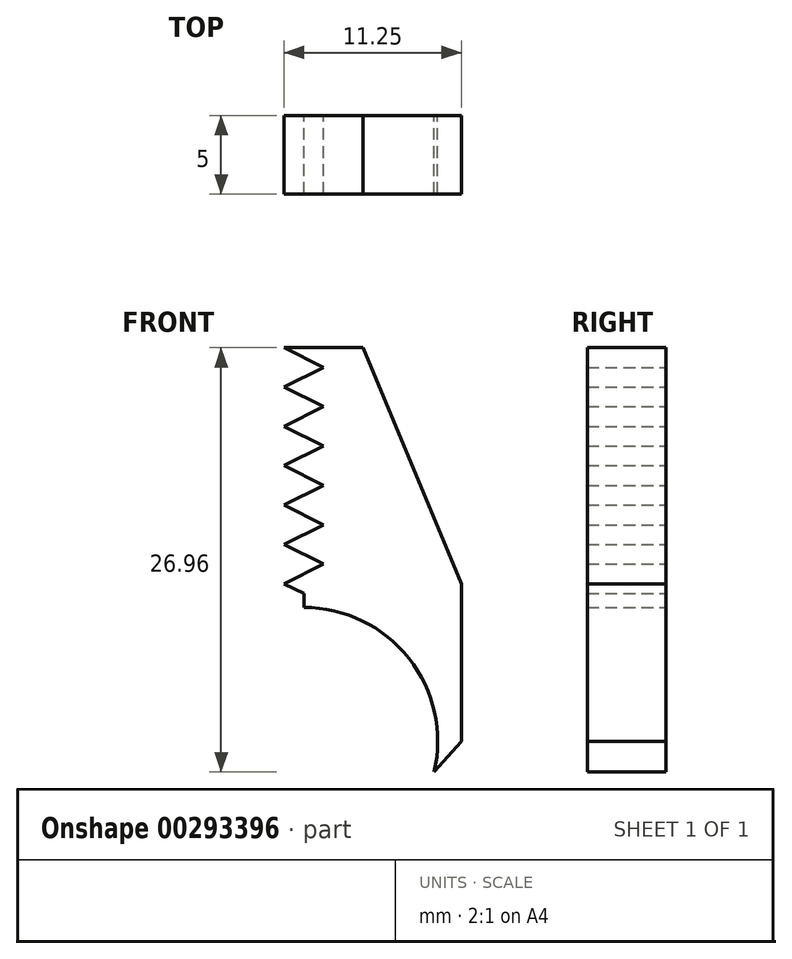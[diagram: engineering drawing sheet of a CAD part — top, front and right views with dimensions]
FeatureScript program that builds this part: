
annotation { "Feature Type Name" : "Feature", "Feature Type Description" : "" }
export const myFeature = defineFeature(function(context is Context, id is Id, definition is map)
    precondition{}
    {
        {
            var Q0;
            Q0=qCreatedBy(makeId("Front.planeOp"),FACE);
            var sketch = newSketch(context, id + "F0", { "sketchPlane" : qUnion([Q0])});
            skArc(sketch, "E0", {"start": v(0, 7.5) * mm, "mid": v(-6.84, -3.09) * mm, "end": v(5.63, -4.96) * mm});
            skLineSegment(sketch, "E1", {"start": v(0, 7.5) * mm, "end": v(0, 9.13) * mm});
            skLineSegment(sketch, "E2", {"start": v(0, 9.13) * mm, "end": v(1.25, 10) * mm});
            skLineSegment(sketch, "E3", {"start": v(1.25, 10) * mm, "end": v(1.25, 25) * mm});
            skLineSegment(sketch, "E4", {"start": v(1.25, 25) * mm, "end": v(3.75, 25) * mm});
            skLineSegment(sketch, "E5", {"start": v(3.75, 25) * mm, "end": v(10, 10) * mm});
            skLineSegment(sketch, "E6", {"start": v(10, 10) * mm, "end": v(10, 0) * mm});
            skLineSegment(sketch, "E7", {"start": v(10, 0) * mm, "end": v(5.62, -4.96) * mm});
            skLineSegment(sketch, "E8", {"start": v(1.25, 25) * mm, "end": v(1.25, 10) * mm});
            skLineSegment(sketch, "E9", {"start": v(1.25, 10) * mm, "end": v(10, 10) * mm, "construction": true});
            skLineSegment(sketch, "E10", {"start": v(0, 0) * mm, "end": v(10, 0) * mm, "construction": true});
            skLineSegment(sketch, "E11", {"start": v(0, 9.13) * mm, "end": v(0, 25) * mm, "construction": true});
            skSolve(sketch);
        }
        {
            var Q0;
            Q0=makeQuery(id+"F0.imprint","IMPRINT",FACE,{"disambiguationData":[TD([[makeQuery(id+"F0.imprint","IMPRINT",EDGE,{"derivedFrom":sQuery(id+"F0.wireOp",EDGE,"E0")}),1.0]])]});
            extrude(context, id + "F1", {"entities" : qUnion([Q0]), "depth" : 5 * mm});
        }
        {
            var Q0;
            Q0=makeQuery(id+"F1.opExtrude","CAP_FACE",FACE,{"disambiguationData":[OSD([sQuery(id+"F0.wireOp",EDGE,"E0"),sQuery(id+"F0.wireOp",EDGE,"E1"),sQuery(id+"F0.wireOp",EDGE,"E2"),sQuery(id+"F0.wireOp",EDGE,"E4"),sQuery(id+"F0.wireOp",EDGE,"E5"),sQuery(id+"F0.wireOp",EDGE,"E6"),sQuery(id+"F0.wireOp",EDGE,"E7"),sQuery(id+"F0.wireOp",EDGE,"E8")])],"isStart":false});
            var sketch = newSketch(context, id + "F2", { "sketchPlane" : qUnion([Q0])});
            skLineSegment(sketch, "E12", {"start": v(1.25, 25) * mm, "end": v(1.25, 22.5) * mm});
            skLineSegment(sketch, "E13", {"start": v(1.25, 23.75) * mm, "end": v(-1.25, 25) * mm});
            skPoint(sketch, "E13.endSnap0", {"position": v(1.25, 23.75) * mm});
            skLineSegment(sketch, "E14", {"start": v(1.25, 9.13) * mm, "end": v(1.25, 24.37) * mm, "construction": true});
            skLineSegment(sketch, "E15.0.1.0", {"start": v(-1.25, 22.5) * mm, "end": v(1.25, 23.75) * mm});
            skLineSegment(sketch, "E15.0.1.1", {"start": v(1.25, 21.25) * mm, "end": v(-1.25, 22.5) * mm});
            skLineSegment(sketch, "E15.0.1.2", {"start": v(0, 6.63) * mm, "end": v(0, 7.5) * mm, "construction": true});
            skLineSegment(sketch, "E15.0.2.0", {"start": v(-1.25, 20) * mm, "end": v(1.25, 21.25) * mm});
            skLineSegment(sketch, "E15.0.2.1", {"start": v(1.25, 18.75) * mm, "end": v(-1.25, 20) * mm});
            skLineSegment(sketch, "E15.0.2.2", {"start": v(0, 4.13) * mm, "end": v(0, 8.5) * mm, "construction": true});
            skLineSegment(sketch, "E15.0.3.0", {"start": v(-1.25, 17.5) * mm, "end": v(1.25, 18.75) * mm});
            skLineSegment(sketch, "E15.0.3.1", {"start": v(1.25, 16.25) * mm, "end": v(-1.25, 17.5) * mm});
            skLineSegment(sketch, "E15.0.3.2", {"start": v(0, 1.63) * mm, "end": v(0, 8.5) * mm, "construction": true});
            skLineSegment(sketch, "E15.0.4.0", {"start": v(-1.25, 15) * mm, "end": v(1.25, 16.25) * mm});
            skLineSegment(sketch, "E15.0.4.1", {"start": v(1.25, 13.75) * mm, "end": v(-1.25, 15) * mm});
            skLineSegment(sketch, "E15.0.4.2", {"start": v(0, -0.87) * mm, "end": v(0, 7.5) * mm, "construction": true});
            skLineSegment(sketch, "E15.0.5.0", {"start": v(-1.25, 12.5) * mm, "end": v(1.25, 13.75) * mm});
            skLineSegment(sketch, "E15.0.5.1", {"start": v(1.25, 11.25) * mm, "end": v(-1.25, 12.5) * mm});
            skLineSegment(sketch, "E15.0.5.2", {"start": v(0, -3.37) * mm, "end": v(0, 9.13) * mm, "construction": true});
            skLineSegment(sketch, "E15.direction1", {"start": v(0, 9.13) * mm, "end": v(25, 9.13) * mm, "construction": true});
            skLineSegment(sketch, "E15.direction2", {"start": v(0, 8.5) * mm, "end": v(0, 6.63) * mm, "construction": true});
            skCircle(sketch, "E16", {"center": v(0, 0) * mm, "radius": 7.5 * mm, "construction": true});
            skArc(sketch, "E17.0", {"start": v(8.27, -1.96) * mm, "mid": v(6.67, 5.27) * mm, "end": v(0, 8.5) * mm});
            skLineSegment(sketch, "E18", {"start": v(10, 0) * mm, "end": v(5.63, -4.96) * mm});
            skLineSegment(sketch, "E19.trimOffspring", {"start": v(0, 11.05) * mm, "end": v(0, 24.37) * mm, "construction": true});
            skLineSegment(sketch, "E20.trimOffspring", {"start": v(0, 8.55) * mm, "end": v(0, 9.13) * mm, "construction": true});
            skLineSegment(sketch, "E21", {"start": v(0, 9.13) * mm, "end": v(0, 8.5) * mm});
            skLineSegment(sketch, "E22", {"start": v(10, 0) * mm, "end": v(10, 10) * mm});
            skLineSegment(sketch, "E23", {"start": v(10, 10) * mm, "end": v(3.75, 25) * mm});
            skLineSegment(sketch, "E24", {"start": v(3.75, 25) * mm, "end": v(1.25, 25) * mm});
            skLineSegment(sketch, "E25", {"start": v(1.25, 25) * mm, "end": v(-1.25, 25) * mm});
            skLineSegment(sketch, "E26", {"start": v(1.25, 11.25) * mm, "end": v(1.25, 9.13) * mm, "construction": true});
            skLineSegment(sketch, "E27", {"start": v(1.25, 9.13) * mm, "end": v(1.25, 11.25) * mm, "construction": true});
            skLineSegment(sketch, "E28.0.1.0", {"start": v(-1.25, 10) * mm, "end": v(1.25, 11.25) * mm});
            skLineSegment(sketch, "E28.0.1.1", {"start": v(0, 9.37) * mm, "end": v(-1.25, 10) * mm});
            skLineSegment(sketch, "E28.1.0.0", {"start": v(16.35, 12.5) * mm, "end": v(18.85, 13.75) * mm});
            skLineSegment(sketch, "E28.1.0.1", {"start": v(18.85, 11.25) * mm, "end": v(16.35, 12.5) * mm});
            skLineSegment(sketch, "E28.1.1.0", {"start": v(16.35, 10) * mm, "end": v(18.85, 11.25) * mm});
            skLineSegment(sketch, "E28.1.1.1", {"start": v(18.85, 8.75) * mm, "end": v(16.35, 10) * mm});
            skLineSegment(sketch, "E28.2.0.0", {"start": v(33.95, 12.5) * mm, "end": v(36.45, 13.75) * mm});
            skLineSegment(sketch, "E28.2.0.1", {"start": v(36.45, 11.25) * mm, "end": v(33.95, 12.5) * mm});
            skLineSegment(sketch, "E28.2.1.0", {"start": v(33.95, 10) * mm, "end": v(36.45, 11.25) * mm});
            skLineSegment(sketch, "E28.2.1.1", {"start": v(36.45, 8.75) * mm, "end": v(33.95, 10) * mm});
            skLineSegment(sketch, "E28.direction1", {"start": v(-1.25, 12.5) * mm, "end": v(16.35, 12.5) * mm, "construction": true});
            skLineSegment(sketch, "E28.direction2", {"start": v(-1.25, 12.5) * mm, "end": v(-1.25, 10) * mm, "construction": true});
            skPoint(sketch, "E29.orphan", {"position": v(1.25, 8.75) * mm});
            skLineSegment(sketch, "E30.trimOffspring", {"start": v(0, 9.37) * mm, "end": v(0, 16.87) * mm, "construction": true});
            skLineSegment(sketch, "E31.trimOffspring", {"start": v(0, 9.37) * mm, "end": v(0, 19.37) * mm, "construction": true});
            skLineSegment(sketch, "E32.trimOffspring", {"start": v(0, 9.37) * mm, "end": v(0, 11.87) * mm, "construction": true});
            skLineSegment(sketch, "E33.trimOffspring", {"start": v(0, 9.37) * mm, "end": v(0, 14.37) * mm, "construction": true});
            skLineSegment(sketch, "E34", {"start": v(0, 9.37) * mm, "end": v(0, 9.13) * mm});
            skSolve(sketch);
        }
        {
            var Q0;
            Q0=qSketchRegion(id+"F2",true);
            extrude(context, id + "F3", {"entities" : qUnion([Q0]), "operationType" : NewBodyOperationType.ADD, "depth" : 5 * mm, "hasSecondDirection" : true, "secondDirectionOppositeDirection" : true, "secondDirectionDepth" : 5 * mm});
        }
        {
            var Q0;
            Q0=makeQuery(id+"F1.opExtrude","CAP_FACE",FACE,{"disambiguationData":[OSD([sQuery(id+"F0.wireOp",EDGE,"E0"),sQuery(id+"F0.wireOp",EDGE,"E1"),sQuery(id+"F0.wireOp",EDGE,"E2"),sQuery(id+"F0.wireOp",EDGE,"E4"),sQuery(id+"F0.wireOp",EDGE,"E5"),sQuery(id+"F0.wireOp",EDGE,"E6"),sQuery(id+"F0.wireOp",EDGE,"E7"),sQuery(id+"F0.wireOp",EDGE,"E8")])],"isStart":false});
            var sketch = newSketch(context, id + "F4", { "sketchPlane" : qUnion([Q0])});
            skCircle(sketch, "E35", {"center": v(0, 0) * mm, "radius": 2.5 * mm});
            skSolve(sketch);
        }
        {
            var Q0;
            Q0=makeQuery(id+"F4.imprint","IMPRINT",FACE,{"disambiguationData":[TD([[makeQuery(id+"F4.imprint","IMPRINT",EDGE,{"derivedFrom":sQuery(id+"F4.wireOp",EDGE,"E35")}),1.0]])]});
            extrude(context, id + "F5", {"entities" : qUnion([Q0]), "operationType" : NewBodyOperationType.REMOVE, "endBound" : BoundingType.THROUGH_ALL, "oppositeDirection" : true, "depth" : 25 * mm});
        }
        {
            var Q0;
            Q0=makeQuery(id+"F1.opExtrude","SWEPT_BODY",BODY,{"disambiguationData":[OSD([sQuery(id+"F0.wireOp",EDGE,"E0"),sQuery(id+"F0.wireOp",EDGE,"E1"),sQuery(id+"F0.wireOp",EDGE,"E2"),sQuery(id+"F0.wireOp",EDGE,"E4"),sQuery(id+"F0.wireOp",EDGE,"E5"),sQuery(id+"F0.wireOp",EDGE,"E6"),sQuery(id+"F0.wireOp",EDGE,"E7"),sQuery(id+"F0.wireOp",EDGE,"E8")])]});
            transform(context, id + "F6", {"entities" : qUnion([Q0]), "transformType" : TransformType.TRANSLATION_3D, "dx" : 0 * mm, "dy" : 0 * mm, "dz" : 0 * mm, "makeCopy" : true});
        }
        {
            var Q0;
            Q0=makeQuery(id+"F6.opPattern","COPY",BODY,{"derivedFrom":makeQuery(id+"F1.opExtrude","SWEPT_BODY",BODY,{"disambiguationData":[OSD([sQuery(id+"F0.wireOp",EDGE,"E0"),sQuery(id+"F0.wireOp",EDGE,"E1"),sQuery(id+"F0.wireOp",EDGE,"E2"),sQuery(id+"F0.wireOp",EDGE,"E4"),sQuery(id+"F0.wireOp",EDGE,"E5"),sQuery(id+"F0.wireOp",EDGE,"E6"),sQuery(id+"F0.wireOp",EDGE,"E7"),sQuery(id+"F0.wireOp",EDGE,"E8")])]}),"instanceName":"1"});
            deleteBodies(context, id + "F7", {"entities" : qUnion([Q0])});
        }
        {
            var Q0;
            Q0=makeQuery(id+"F1.opExtrude","SWEPT_BODY",BODY,{"disambiguationData":[OSD([sQuery(id+"F0.wireOp",EDGE,"E0"),sQuery(id+"F0.wireOp",EDGE,"E1"),sQuery(id+"F0.wireOp",EDGE,"E2"),sQuery(id+"F0.wireOp",EDGE,"E4"),sQuery(id+"F0.wireOp",EDGE,"E5"),sQuery(id+"F0.wireOp",EDGE,"E6"),sQuery(id+"F0.wireOp",EDGE,"E7"),sQuery(id+"F0.wireOp",EDGE,"E8")])]});
            transform(context, id + "F8", {"entities" : qUnion([Q0]), "transformType" : TransformType.TRANSLATION_3D, "dx" : 20 * mm, "dy" : 0 * mm, "dz" : 0 * mm, "makeCopy" : true});
        }
        {
            var Q0;
            Q0=makeQuery(id+"F8.opPattern","COPY",BODY,{"derivedFrom":makeQuery(id+"F1.opExtrude","SWEPT_BODY",BODY,{"disambiguationData":[OSD([sQuery(id+"F0.wireOp",EDGE,"E0"),sQuery(id+"F0.wireOp",EDGE,"E1"),sQuery(id+"F0.wireOp",EDGE,"E2"),sQuery(id+"F0.wireOp",EDGE,"E4"),sQuery(id+"F0.wireOp",EDGE,"E5"),sQuery(id+"F0.wireOp",EDGE,"E6"),sQuery(id+"F0.wireOp",EDGE,"E7"),sQuery(id+"F0.wireOp",EDGE,"E8")])]}),"instanceName":"1"});
            deleteBodies(context, id + "F9", {"entities" : qUnion([Q0])});
        }
        {
            var Q0;
            Q0=makeQuery(id+"F1.opExtrude","SWEPT_BODY",BODY,{"disambiguationData":[OSD([sQuery(id+"F0.wireOp",EDGE,"E0"),sQuery(id+"F0.wireOp",EDGE,"E1"),sQuery(id+"F0.wireOp",EDGE,"E2"),sQuery(id+"F0.wireOp",EDGE,"E4"),sQuery(id+"F0.wireOp",EDGE,"E5"),sQuery(id+"F0.wireOp",EDGE,"E6"),sQuery(id+"F0.wireOp",EDGE,"E7"),sQuery(id+"F0.wireOp",EDGE,"E8")])]});
            transform(context, id + "F10", {"entities" : qUnion([Q0]), "transformType" : TransformType.TRANSLATION_3D, "dx" : 0 * mm, "dy" : 0 * mm, "dz" : 0 * mm, "makeCopy" : true});
        }
        {
            var Q0;
            Q0=makeQuery(id+"F10.opPattern","COPY",BODY,{"derivedFrom":makeQuery(id+"F1.opExtrude","SWEPT_BODY",BODY,{"disambiguationData":[OSD([sQuery(id+"F0.wireOp",EDGE,"E0"),sQuery(id+"F0.wireOp",EDGE,"E1"),sQuery(id+"F0.wireOp",EDGE,"E2"),sQuery(id+"F0.wireOp",EDGE,"E4"),sQuery(id+"F0.wireOp",EDGE,"E5"),sQuery(id+"F0.wireOp",EDGE,"E6"),sQuery(id+"F0.wireOp",EDGE,"E7"),sQuery(id+"F0.wireOp",EDGE,"E8")])]}),"instanceName":"1"});
            deleteBodies(context, id + "F11", {"entities" : qUnion([Q0])});
        }
        {
            var Q0;
            Q0=makeQuery(id+"F0.imprint","IMPRINT",FACE,{"disambiguationData":[TD([[makeQuery(id+"F0.imprint","IMPRINT",EDGE,{"derivedFrom":sQuery(id+"F0.wireOp",EDGE,"E0")}),1.0]])]});
            var sketch = newSketch(context, id + "F12", { "sketchPlane" : qUnion([Q0])});
            skLineSegment(sketch, "E36.bottom", {"start": v(27.39, 30.34) * mm, "end": v(-29.72, 30.34) * mm});
            skLineSegment(sketch, "E36.top", {"start": v(27.39, -12.98) * mm, "end": v(-29.72, -12.98) * mm});
            skLineSegment(sketch, "E36.left", {"start": v(27.39, 30.34) * mm, "end": v(27.39, -12.98) * mm});
            skLineSegment(sketch, "E36.right", {"start": v(-29.72, 30.34) * mm, "end": v(-29.72, -12.98) * mm});
            skSolve(sketch);
        }
        {
            var Q0;
            Q0 = qSketchRegion(id + "F12", true);
            extrude(context, id + "F13", {"entities" : qUnion([Q0]), "operationType" : NewBodyOperationType.REMOVE, "depth" : 5 * mm});
        }
    });
